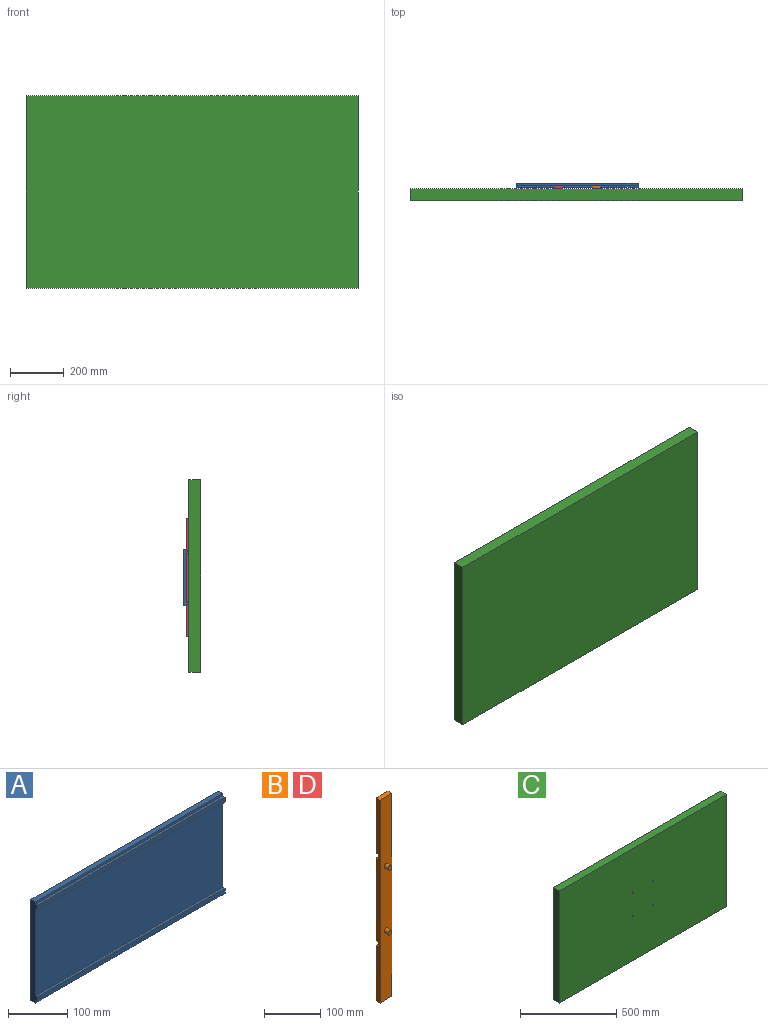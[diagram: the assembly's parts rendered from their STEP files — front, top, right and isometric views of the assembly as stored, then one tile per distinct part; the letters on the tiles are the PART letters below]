
ASSEMBLY  parts=4 mates=7
PART A: 14 faces, bbox 450x15x210 mm
  f0: plane 450x5mm, normal (0,-1,0), area 2250mm2, adj f2,f3,f4,f11
  f1: plane 450x5mm, normal (0,-1,0), area 2250mm2, adj f2,f4,f5,f9
  f2: plane 210x15mm, normal (-1,0,0), area 2200mm2, adj f0,f1,f3,f5,f6,f7,f8,f9
  f3: plane 450x10mm, normal (0,0,-1), area 4500mm2, adj f0,f2,f4,f7
  f4: plane 210x15mm, normal (1,0,0), area 2200mm2, adj f0,f1,f3,f5,f6,f7,f8,f9
  f5: plane 450x10mm, normal (0,0,1), area 4500mm2, adj f1,f2,f4,f7
  f6: plane 450x180mm, normal (0,-1,0), area 81000mm2, adj f2,f4,f8,f12
  f7: plane 450x210mm, normal (0,1,0), area 94500mm2, adj f2,f3,f4,f5
  f8: plane 450x5mm, normal (0,0,-1), area 2250mm2, adj f2,f4,f6,f10
  f9: plane 450x5mm, normal (0,0,1), area 2250mm2, adj f1,f2,f4,f10
  f10: plane 450x10mm, normal (0,-1,0), area 4500mm2, adj f2,f4,f8,f9
  f11: plane 450x5mm, normal (0,0,-1), area 2250mm2, adj f0,f2,f4,f13
  f12: plane 450x5mm, normal (0,0,1), area 2250mm2, adj f2,f4,f6,f13
  f13: plane 450x10mm, normal (0,-1,0), area 4500mm2, adj f2,f4,f11,f12
PART B: 18 faces, bbox 30x20x440 mm
  f0: plane 180x30mm, normal (0,1,0), area 5400mm2, adj f2,f4,f12,f15
  f1: plane 120x30mm, normal (0,1,0), area 3600mm2, adj f2,f4,f5,f16
  f2: plane 440x10mm, normal (-1,0,0), area 4300mm2, adj f0,f1,f3,f5,f6,f7,f12,f13
  f3: plane 30x10mm, normal (0,0,-1), area 300mm2, adj f2,f4,f6,f7
  f4: plane 440x10mm, normal (1,0,0), area 4300mm2, adj f0,f1,f3,f5,f6,f7,f12,f13
  f5: plane 30x10mm, normal (0,0,1), area 300mm2, adj f1,f2,f4,f6
  f6: plane 440x30mm, normal (0,-1,0), area 13042.9mm2, adj f2,f3,f4,f5,f8,f10
  f7: plane 120x30mm, normal (0,1,0), area 3600mm2, adj f2,f3,f4,f13
  f8: cylinder r=5mm len=10mm, axis (0,1,0), area 314.2mm2, adj f6,f9
  f9: plane 10x10mm, normal (0,-1,0), area 78.5mm2, adj f8
  f10: cylinder r=5mm len=10mm, axis (0,1,0), area 314.2mm2, adj f6,f11
  f11: plane 10x10mm, normal (0,-1,0), area 78.5mm2, adj f10
  f12: plane 30x5mm, normal (0,0,-1), area 150mm2, adj f0,f2,f4,f14
  f13: plane 30x5mm, normal (0,0,1), area 150mm2, adj f2,f4,f7,f14
  f14: plane 30x10mm, normal (0,1,0), area 300mm2, adj f2,f4,f12,f13
  f15: plane 30x5mm, normal (0,0,1), area 150mm2, adj f0,f2,f4,f17
  f16: plane 30x5mm, normal (0,0,-1), area 150mm2, adj f1,f2,f4,f17
  f17: plane 30x10mm, normal (0,1,0), area 300mm2, adj f2,f4,f15,f16
PART C: 14 faces, bbox 1231x44x714 mm
  f0: plane 714x44mm, normal (-1,0,0), area 31416mm2, adj f1,f3,f4,f5
  f1: plane 1231x44mm, normal (0,0,-1), area 54164mm2, adj f0,f2,f4,f5
  f2: plane 714x44mm, normal (1,0,0), area 31416mm2, adj f1,f3,f4,f5
  f3: plane 1231x44mm, normal (0,0,1), area 54164mm2, adj f0,f2,f4,f5
  f4: plane 1231x714mm, normal (0,-1,0), area 878619.8mm2, adj f0,f1,f2,f3,f6,f8,f10,f12
  f5: plane 1231x714mm, normal (0,1,0), area 878934mm2, adj f0,f1,f2,f3
  f6: cylinder r=5mm len=10mm, axis (0,-1,0), area 314.2mm2, adj f4,f7
  f7: plane 10x10mm, normal (0,-1,0), area 78.5mm2, adj f6
  f8: cylinder r=5mm len=10mm, axis (0,-1,0), area 314.2mm2, adj f4,f9
  f9: plane 10x10mm, normal (0,-1,0), area 78.5mm2, adj f8
  f10: cylinder r=5mm len=10mm, axis (0,-1,0), area 314.2mm2, adj f4,f11
  f11: plane 10x10mm, normal (0,-1,0), area 78.5mm2, adj f10
  f12: cylinder r=5mm len=10mm, axis (0,-1,0), area 314.2mm2, adj f4,f13
  f13: plane 10x10mm, normal (0,-1,0), area 78.5mm2, adj f12
PART D: same geometry as B
PLACE A t=(-224.12,7.74,-105.4)mm fixed
PLACE B t=(55.88,-2.26,-220.4)mm
PLACE C rot(axis=(1,0,0),180deg) t=(-619.62,-56.26,361.6)mm
PLACE D t=(-84.12,-2.26,-220.4)mm
MATE planar C.f4 <-> B.f6  axis (0,1,0) through (-4.12,-12.26,4.6)mm
MATE planar A.f10 <-> D.f17  axis (0,-1,0) through (0.88,-7.26,94.6)mm
MATE planar D.f16 <-> A.f9  axis (0,0,-1) through (-69.12,-4.76,99.6)mm
MATE planar B.f17 <-> A.f10  axis (0,1,0) through (70.88,-7.26,94.6)mm
MATE cylindrical C.f8 <-> B.f10  axis (0,1,0) through (70.88,-17.26,-70.4)mm
MATE parallel C.f1 <-> A.f5  axis (0,0,1) through (-4.12,-34.26,361.6)mm
MATE planar B.f15 <-> A.f8  axis (0,0,1) through (70.88,-4.76,89.6)mm
